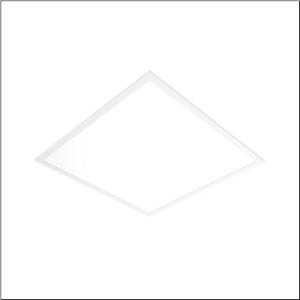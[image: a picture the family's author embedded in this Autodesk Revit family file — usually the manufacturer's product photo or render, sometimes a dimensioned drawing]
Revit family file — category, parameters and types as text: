
# Revit family: apollon_r__41_51mh12w72622_4ebd
name_source: partatom
category: Lighting Fixtures
units: mm (PartAtom-declared; Revit-internal decimal feet)

## family parameters
Cut with Voids When Loaded = No
Host = Face
Light Source = No
Part Type = Normal
Room Calculation Point = No
Round Connector Dimension = Use Diameter
Shared = No

## types (1)
- Apollon® 41 (1 x LED, 3700 lm, 35 W, 6500K)
    Apparent Load = 35 VA
    CIE Flux Codes = 63 87 97 100 100
    Color Rendering = 80
    Color Temperature = 6500K
    Default Elevation = 1800 mm
    Description = Apollon® 41, office luminaire, primary optical cover: prismatic diffuser, of PS, light emission: direct distribution, primary light characteristic: symmetric, installation type: lay-in mounting, LED, rated luminous flux: 3.700lm, luminous efficacy: 105lm/W, light colour: 865, colour temperature: 6500K, control gear: ON/OFF, with terminal, 3-pole, mains connection: 220..240V, AC, 50/60Hz, rated input power: 35W, housing, of aluminium section, traffic white (RAL 9016), module: M600, length: 595mm, width: 595mm, height: 32mm, housing upper side, of sheet steel, protection rating (complete): IP20, protection rating (lamp compartment, on room side): IP40, insulation class (complete): insulation class II (safety insulation), certification: CE, ENEC, permissible operating ambient temperature: -20..+40°C, packaging unit: 1 piece
    Height = 0 mm  [stored 0 ft]
    Lamp = 1 x LED
    Lamp Light Flux = 3700 lm
    Lamp Power = 35 W
    Lamp count = 1
    Length = 596 mm
    Luminous efficacy = 106 lm/W
    Manufacturer = Siteco
    ModVariant = No
    Model = 51MH12W72622
    Mounting Place = Ceiling
    Mounting Type = Recessed
    Number of Poles = 1
    OnlyDefault = Yes
    Power Factor = 1
    Product Name = Apollon® 41
    Product group = office luminaire | ceiling recessed
    ProductGroupID = 400
    Protection Class = Protection class II
    Protection Degree = IP 20
    RLX_Detail_Level = 1
    RLX_Emergency_Light_Flux = 0 lm
    RLX_Emergency_Type = 0
    RLX_Emergency_Type_DB = No
    RlxData = <blob elided: 14869 chars, md5=b9bb901e>
    Socket = socket
    Standby Power = 0 W
    System Light Flux = 3700 lm
    System Power = 35 W
    Type Comments = Product without accessories
    Type Image = l_1291024.jpg
    URL = http://relux.com
    VarID = ---
    Voltage = 0 V
    Weight = 0.00 kg
    Width = 596 mm

note: [stored X ft] marks values corroborated as IEEE doubles in the binary element streams (Revit-internal decimal feet)

## geometry (parser evidence)
native form markers: Sweep x12
no freeform markers — native parametric forms only
